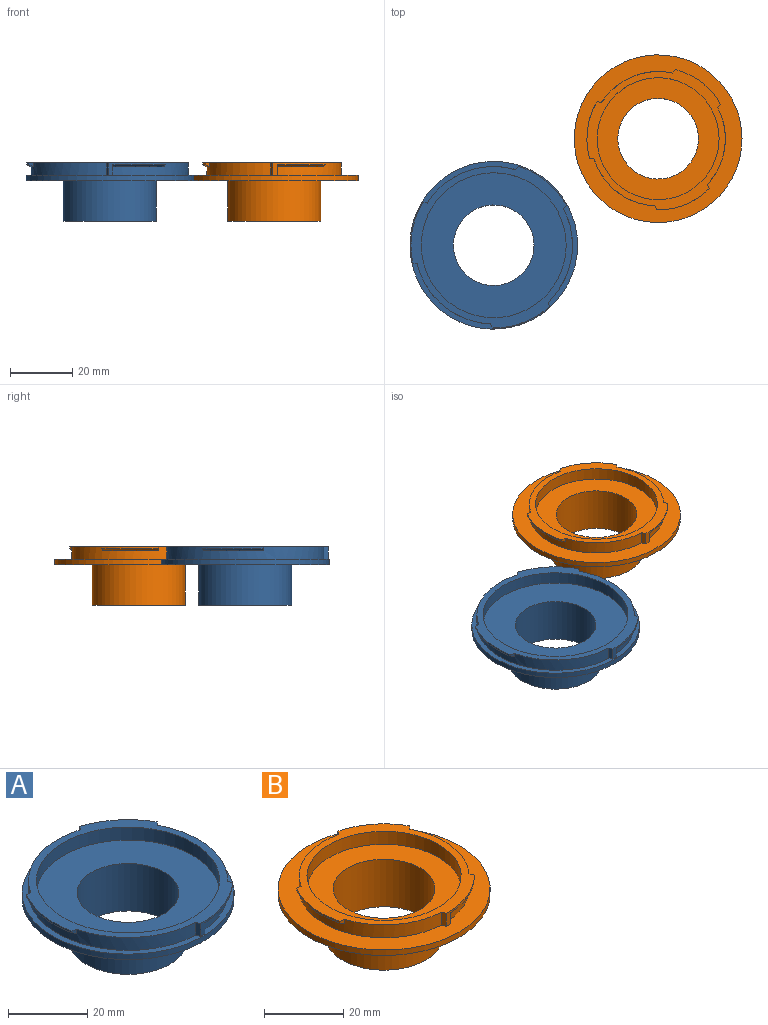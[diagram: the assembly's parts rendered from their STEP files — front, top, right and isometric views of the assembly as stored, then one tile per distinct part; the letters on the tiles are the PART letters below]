
ASSEMBLY  parts=2 mates=1
PART A: 23 faces, bbox 53.7x53.7x18.7 mm
  f0: plane 51.82x51.75mm, normal (0,0,1), area 382.8mm2, adj f2,f4,f5,f15,f16,f17,f18,f19
  f1: revolved ~20.44x5.2mm, area 30.3mm2, adj f2,f15,f21,f22
  f2: cylinder r=26.5mm len=19.43mm, axis (0,0,-1), area 11.1mm2, adj f0,f1,f21,f22
  f3: revolved ~16.36x13.74mm, area 30.3mm2, adj f4,f15,f19,f20
  f4: cylinder r=26.5mm len=15.24mm, axis (0,0,-1), area 11.1mm2, adj f0,f3,f19,f20
  f5: cylinder r=26.5mm len=18.42mm, axis (0,0,-1), area 16.4mm2, adj f0,f6,f7,f8,f17,f18
  f6: revolved ~17.42x8.25mm, area 27.6mm2, adj f5,f7,f15,f17
  f7: plane 3.45x1.3mm, normal (1,0,0), area 4mm2, adj f5,f6,f8,f15
  f8: plane 53.7x53.7mm, normal (0,0,1), area 267.5mm2, adj f5,f7,f13,f15,f18
  f9: plane 46.4x46.4mm, normal (0,0,1), area 1168.1mm2, adj f10,f16
  f10: cylinder r=12.9mm len=25.8mm, axis (0,0,-1), area 1191.3mm2, adj f9,f12
  f11: cylinder r=14.9mm len=29.8mm, axis (0,0,-1), area 1217.1mm2, adj f12,f14
  f12: plane 29.8x29.8mm, normal (0,0,-1), area 174.7mm2, adj f10,f11
  f13: cylinder r=26.85mm len=53.7mm, axis (0,0,-1), area 286.5mm2, adj f8,f14
  f14: plane 53.7x53.7mm, normal (0,0,-1), area 1567.4mm2, adj f11,f13
  f15: cylinder r=25.2mm len=50.4mm, axis (0,0,-1), area 548.9mm2, adj f0,f1,f3,f6,f7,f8,f17,f18
  f16: cylinder r=23.2mm len=46.4mm, axis (0,0,-1), area 583.1mm2, adj f0,f9
  f17: plane 1.33x1.32mm, normal (0.94,0.35,0), area 1.3mm2, adj f0,f5,f6,f15
  f18: plane 4x1.31mm, normal (-0.94,-0.35,0), area 5.6mm2, adj f0,f5,f8,f15
  f19: plane 1.32x1.1mm, normal (-0.77,0.63,0), area 1.3mm2, adj f0,f3,f4,f15
  f20: plane 1.31x1.1mm, normal (0.77,-0.63,0), area 1.3mm2, adj f0,f3,f4,f15
  f21: plane 1.4x1.32mm, normal (-0.16,-0.99,0), area 1.3mm2, adj f0,f1,f2,f15
  f22: plane 1.4x1.31mm, normal (0.16,0.99,0), area 1.3mm2, adj f0,f1,f2,f15
PART B: 23 faces, bbox 53.7x53.7x18.7 mm
  f0: plane 44.98x44.38mm, normal (0,0,1), area 330.8mm2, adj f2,f4,f5,f15,f16,f17,f18,f19
  f1: revolved ~19.12x4.71mm, area 28.1mm2, adj f2,f15,f21,f22
  f2: cylinder r=22.81mm len=18.02mm, axis (0,0,-1), area 10.3mm2, adj f0,f1,f21,f22
  f3: revolved ~15.51x12.41mm, area 28.1mm2, adj f4,f15,f19,f20
  f4: cylinder r=22.81mm len=14.39mm, axis (0,0,-1), area 10.3mm2, adj f0,f3,f19,f20
  f5: cylinder r=22.81mm len=16.83mm, axis (0,0,-1), area 15.5mm2, adj f0,f6,f7,f8,f17,f18
  f6: revolved ~15.9x8.2mm, area 25.5mm2, adj f5,f7,f15,f17
  f7: plane 3.45x1.3mm, normal (1,0,0), area 4mm2, adj f5,f6,f8,f15
  f8: plane 53.7x53.7mm, normal (0,0,1), area 808.3mm2, adj f5,f7,f13,f15,f18
  f9: plane 39.03x39.03mm, normal (0,0,1), area 673.6mm2, adj f10,f16
  f10: cylinder r=12.9mm len=25.8mm, axis (0,0,-1), area 1191.3mm2, adj f9,f12
  f11: cylinder r=14.9mm len=29.8mm, axis (0,0,-1), area 1217.1mm2, adj f12,f14
  f12: plane 29.8x29.8mm, normal (0,0,-1), area 174.7mm2, adj f10,f11
  f13: cylinder r=26.85mm len=53.7mm, axis (0,0,-1), area 286.5mm2, adj f8,f14
  f14: plane 53.7x53.7mm, normal (0,0,-1), area 1567.4mm2, adj f11,f13
  f15: cylinder r=21.52mm len=43.03mm, axis (0,0,-1), area 462mm2, adj f0,f1,f3,f6,f7,f8,f17,f18
  f16: cylinder r=19.52mm len=39.03mm, axis (0,0,-1), area 490.5mm2, adj f0,f9
  f17: plane 1.34x1.32mm, normal (0.93,0.38,0), area 1.3mm2, adj f0,f5,f6,f15
  f18: plane 4x1.32mm, normal (-0.93,-0.38,0), area 5.7mm2, adj f0,f5,f8,f15
  f19: plane 1.32x1.15mm, normal (-0.79,0.61,0), area 1.3mm2, adj f0,f3,f4,f15
  f20: plane 1.32x1.14mm, normal (0.79,-0.61,0), area 1.3mm2, adj f0,f3,f4,f15
  f21: plane 1.43x1.32mm, normal (-0.13,-0.99,0), area 1.3mm2, adj f0,f1,f2,f15
  f22: plane 1.43x1.32mm, normal (0.13,0.99,0), area 1.3mm2, adj f0,f1,f2,f15
PLACE A t=(-1.39,8.85,8.78)mm fixed
PLACE B t=(51.25,42.96,8.78)mm
MATE planar B.f16 <-> A.f16  axis (0,0,-1) through (51.25,42.96,8.78)mm
